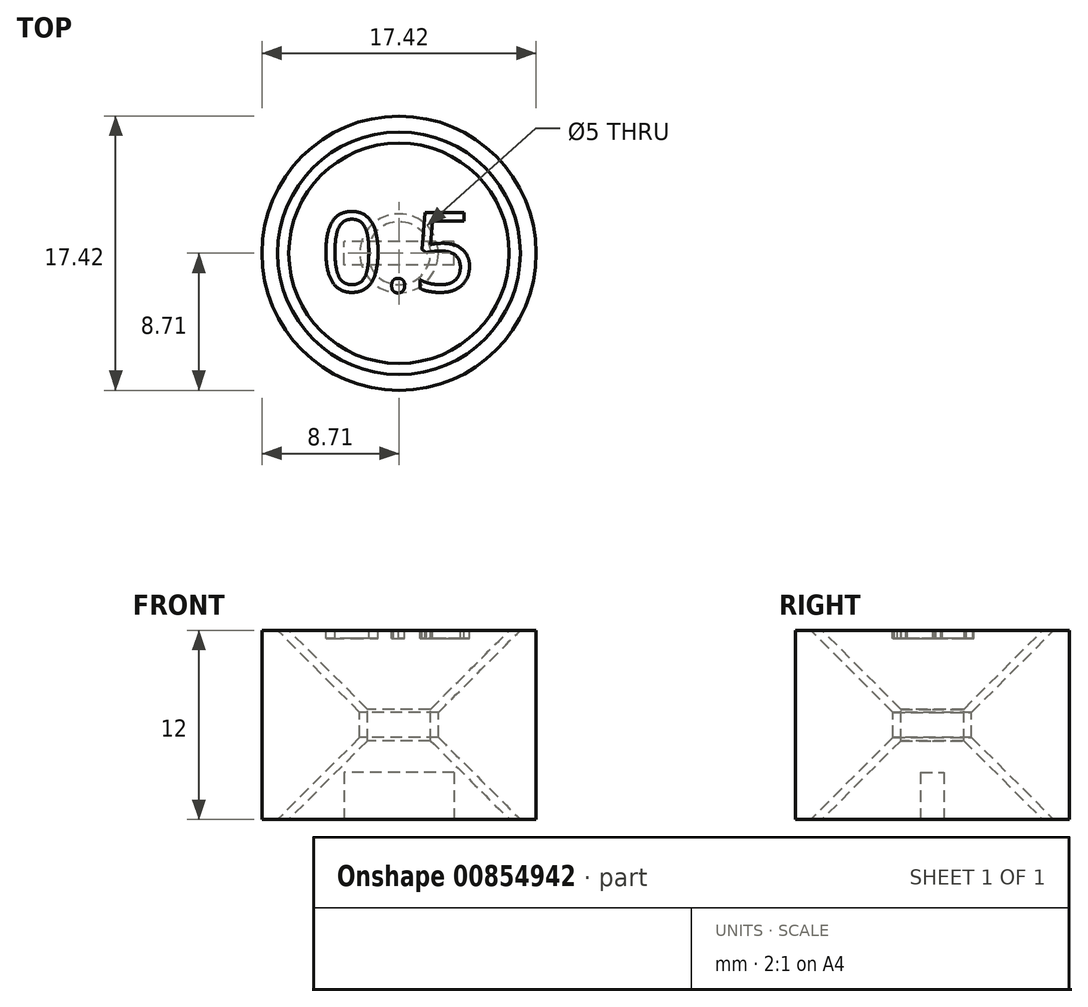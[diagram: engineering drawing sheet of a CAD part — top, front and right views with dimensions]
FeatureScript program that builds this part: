
annotation { "Feature Type Name" : "Feature", "Feature Type Description" : "" }
export const myFeature = defineFeature(function(context is Context, id is Id, definition is map)
    precondition{}
    {
        {
            var Q0;
            Q0=qCreatedBy(makeId("Front.planeOp"),FACE);
            var sketch = newSketch(context, id + "F0", { "sketchPlane" : qUnion([Q0])});
            skLineSegment(sketch, "E0", {"start": v(0, 0) * mm, "end": v(7, 0) * mm});
            skLineSegment(sketch, "E1", {"start": v(7, 0) * mm, "end": v(2, 5) * mm});
            skLineSegment(sketch, "E2", {"start": v(2, 5) * mm, "end": v(2, 7) * mm});
            skLineSegment(sketch, "E3", {"start": v(2, 7) * mm, "end": v(7, 12) * mm});
            skLineSegment(sketch, "E4", {"start": v(7, 12) * mm, "end": v(0, 12) * mm});
            skLineSegment(sketch, "E5", {"start": v(0, 12) * mm, "end": v(0, 0) * mm});
            skLineSegment(sketch, "E6", {"start": v(7.7, 0) * mm, "end": v(2.5, 5.2) * mm});
            skLineSegment(sketch, "E7", {"start": v(2.5, 5.2) * mm, "end": v(2.5, 6.8) * mm});
            skLineSegment(sketch, "E8", {"start": v(7.7, 12) * mm, "end": v(8.7, 12) * mm});
            skLineSegment(sketch, "E9", {"start": v(8.7, 0) * mm, "end": v(7.7, 0) * mm});
            skLineSegment(sketch, "E10", {"start": v(8.7, 0) * mm, "end": v(8.7, 12) * mm});
            skLineSegment(sketch, "E11", {"start": v(7.7, 12) * mm, "end": v(2.5, 6.8) * mm});
            skSolve(sketch);
        }
        {
            var Q0;
            Q0=makeQuery(id+"F0.imprint","IMPRINT",FACE,{"disambiguationData":[TD([[makeQuery(id+"F0.imprint","IMPRINT",EDGE,{"derivedFrom":sQuery(id+"F0.wireOp",EDGE,"E0")}),1.0]])]});
            var Q1;
            Q1=makeQuery(id+"F0.imprint","IMPRINT",FACE,{"disambiguationData":[TD([[makeQuery(id+"F0.imprint","IMPRINT",EDGE,{"derivedFrom":sQuery(id+"F0.wireOp",EDGE,"E6")}),-1.0]])]});
            var Q2;
            Q2=sQuery(id+"F0.wireOp",EDGE,"E5");
            revolve(context, id + "F1", {"surfaceOperationType" : NewSurfaceOperationType.NEW, "entities" : qUnion([Q0, Q1]), "axis" : qUnion([Q2]), "revolveType" : RevolveType.FULL});
        }
        {
            var Q0;
            Q0=makeQuery(id+"F1.opRevolve","SWEPT_FACE",FACE,{"disambiguationData":[OSD([sQuery(id+"F0.wireOp",EDGE,"E4")])]});
            var sketch = newSketch(context, id + "F2", { "sketchPlane" : qUnion([Q0])});
            skText(sketch, "E12", { "text": "0.5", "fontName": "OpenSans-Regular.ttf"});
            const initialGuessF2  = {"E12": [-0.00499, -0.00242, 1, 0, 0.00504]};
            skSetInitialGuess(sketch, initialGuessF2);
            skSolve(sketch);
        }
        {
            var Q0;
            Q0 = qSketchRegion(id + "F2", true);
            extrude(context, id + "F3", {"entities" : qUnion([Q0]), "operationType" : NewBodyOperationType.REMOVE, "oppositeDirection" : true, "depth" : 0.5 * mm, "offsetDistance" : 25 * mm});
        }
        {
            var Q0;
            Q0=makeQuery(id+"F1.opRevolve","SWEPT_FACE",FACE,{"disambiguationData":[OSD([sQuery(id+"F0.wireOp",EDGE,"E0")])]});
            var sketch = newSketch(context, id + "F4", { "sketchPlane" : qUnion([Q0])});
            skLineSegment(sketch, "E13.bottom", {"start": v(3.5, 0.75) * mm, "end": v(-3.5, 0.75) * mm});
            skLineSegment(sketch, "E13.top", {"start": v(3.5, -0.75) * mm, "end": v(-3.5, -0.75) * mm});
            skLineSegment(sketch, "E13.left", {"start": v(3.5, 0.75) * mm, "end": v(3.5, -0.75) * mm});
            skLineSegment(sketch, "E13.right", {"start": v(-3.5, 0.75) * mm, "end": v(-3.5, -0.75) * mm});
            skPoint(sketch, "E13.middle", {"position": v(0, 0) * mm});
            skSolve(sketch);
        }
        {
            var Q0;
            Q0=makeQuery(id+"F4.imprint","IMPRINT",FACE,{"disambiguationData":[TD([[makeQuery(id+"F4.imprint","IMPRINT",EDGE,{"derivedFrom":sQuery(id+"F4.wireOp",EDGE,"E13.bottom")}),1.0]])]});
            extrude(context, id + "F5", {"entities" : qUnion([Q0]), "operationType" : NewBodyOperationType.REMOVE, "oppositeDirection" : true, "depth" : 3 * mm, "offsetDistance" : 25 * mm});
        }
    });
